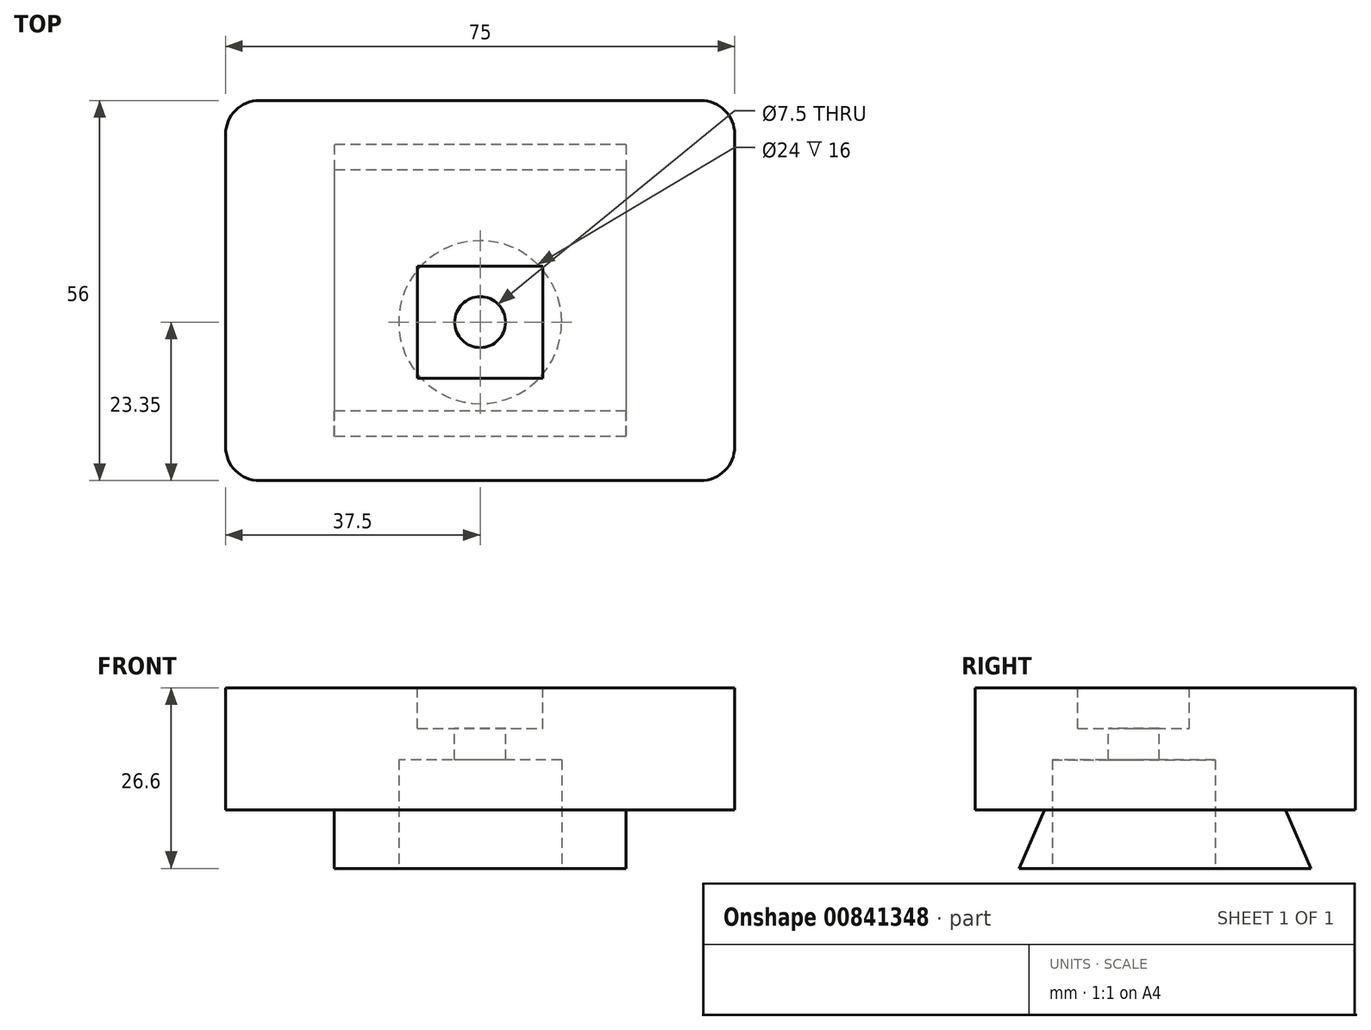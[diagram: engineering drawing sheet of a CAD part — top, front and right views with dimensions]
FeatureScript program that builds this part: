
annotation { "Feature Type Name" : "Feature", "Feature Type Description" : "" }
export const myFeature = defineFeature(function(context is Context, id is Id, definition is map)
    precondition{}
    {
        {
            var Q0;
            Q0=qCreatedBy(makeId("Top.planeOp"),FACE);
            cPlane(context, id + "F0", {"entities" : qUnion([Q0]), "cplaneType" : CPlaneType.OFFSET, "offset" : 8.6 * mm, "oppositeDirection" : true, "width" : 150 * mm, "height" : 150 * mm});
        }
        {
            var Q0;
            Q0=qCreatedBy(makeId("Front.planeOp"),FACE);
            var sketch = newSketch(context, id + "F1", { "sketchPlane" : qUnion([Q0])});
            skLineSegment(sketch, "E0", {"start": v(0, 112.1) * mm, "end": v(0, -117.82) * mm, "construction": true});
            skLineSegment(sketch, "E1", {"start": v(100.36, 0) * mm, "end": v(-122.56, 0) * mm, "construction": true});
            skSolve(sketch);
        }
        {
            var Q0;
            Q0=qCreatedBy(makeId("Top.planeOp"),FACE);
            var sketch = newSketch(context, id + "F2", { "sketchPlane" : qUnion([Q0])});
            skLineSegment(sketch, "E2", {"start": v(0, 30.48) * mm, "end": v(0, -32.87) * mm, "construction": true});
            skLineSegment(sketch, "E3", {"start": v(-42.52, -4.65) * mm, "end": v(39.67, -4.65) * mm, "construction": true});
            skSolve(sketch);
        }
        {
            var Q0;
            Q0=qCreatedBy(id+"F0.planeOp",FACE);
            var sketch = newSketch(context, id + "F3", { "sketchPlane" : qUnion([Q0])});
            skLineSegment(sketch, "E4.bottom", {"start": v(21.5, 21.5) * mm, "end": v(-21.5, 21.5) * mm});
            skLineSegment(sketch, "E4.top", {"start": v(21.5, -21.5) * mm, "end": v(-21.5, -21.5) * mm});
            skLineSegment(sketch, "E4.left", {"start": v(21.5, 21.5) * mm, "end": v(21.5, -21.5) * mm});
            skLineSegment(sketch, "E4.right", {"start": v(-21.5, 21.5) * mm, "end": v(-21.5, -21.5) * mm});
            skPoint(sketch, "E4.middle", {"position": v(0, 0) * mm});
            skSolve(sketch);
        }
        {
            var Q0;
            Q0=qCreatedBy(makeId("Top.planeOp"),FACE);
            var sketch = newSketch(context, id + "F4", { "sketchPlane" : qUnion([Q0])});
            skLineSegment(sketch, "E5.bottom", {"start": v(21.5, 17.75) * mm, "end": v(-21.5, 17.75) * mm});
            skLineSegment(sketch, "E5.top", {"start": v(21.5, -17.75) * mm, "end": v(-21.5, -17.75) * mm});
            skLineSegment(sketch, "E5.left", {"start": v(21.5, 17.75) * mm, "end": v(21.5, -17.75) * mm});
            skLineSegment(sketch, "E5.right", {"start": v(-21.5, 17.75) * mm, "end": v(-21.5, -17.75) * mm});
            skPoint(sketch, "E5.middle", {"position": v(0, 0) * mm});
            skSolve(sketch);
        }
        {
            var Q0;
            Q0 = qSketchRegion(id + "F3", true);
            var Q1;
            Q1 = qSketchRegion(id + "F4", true);
            loft(context, id + "F5", {"sheetProfilesArray" : [{ "sheetProfileEntities" : qUnion([Q0]) }, { "sheetProfileEntities" : qUnion([Q1]) }]});
        }
        {
            var Q0;
            Q0=qCreatedBy(makeId("Top.planeOp"),FACE);
            var sketch = newSketch(context, id + "F6", { "sketchPlane" : qUnion([Q0])});
            skLineSegment(sketch, "E6.bottom", {"start": v(37.5, 28) * mm, "end": v(-37.5, 28) * mm});
            skLineSegment(sketch, "E6.top", {"start": v(37.5, -28) * mm, "end": v(-37.5, -28) * mm});
            skLineSegment(sketch, "E6.left", {"start": v(37.5, 28) * mm, "end": v(37.5, -28) * mm});
            skLineSegment(sketch, "E6.right", {"start": v(-37.5, 28) * mm, "end": v(-37.5, -28) * mm});
            skPoint(sketch, "E6.middle", {"position": v(0, 0) * mm});
            skSolve(sketch);
        }
        {
            var Q0;
            Q0 = qSketchRegion(id + "F6", true);
            extrude(context, id + "F7", {"entities" : qUnion([Q0]), "operationType" : NewBodyOperationType.ADD, "depth" : 18 * mm, "offsetDistance" : 25 * mm});
        }
        {
            var Q0;
            Q0=makeQuery(id+"F7.opExtrude","SWEPT_EDGE",EDGE,{"disambiguationData":[OSD([sQuery(id+"F6.wireOp",EDGE,"E6.bottom"),sQuery(id+"F6.wireOp",EDGE,"E6.right")])]});
            var Q1;
            Q1=makeQuery(id+"F7.opExtrude","SWEPT_EDGE",EDGE,{"disambiguationData":[OSD([sQuery(id+"F6.wireOp",EDGE,"E6.bottom"),sQuery(id+"F6.wireOp",EDGE,"E6.left")])]});
            var Q2;
            Q2=makeQuery(id+"F7.opExtrude","SWEPT_EDGE",EDGE,{"disambiguationData":[OSD([sQuery(id+"F6.wireOp",EDGE,"E6.top"),sQuery(id+"F6.wireOp",EDGE,"E6.left")])]});
            var Q3;
            Q3=makeQuery(id+"F7.opExtrude","SWEPT_EDGE",EDGE,{"disambiguationData":[OSD([sQuery(id+"F6.wireOp",EDGE,"E6.top"),sQuery(id+"F6.wireOp",EDGE,"E6.right")])]});
            fillet(context, id + "F8", {"entities" : qUnion([Q0, Q1, Q2, Q3]), "radius" : 5 * mm, "tangentPropagation" : true, "allowEdgeOverflow" : false});
        }
        {
            var Q0;
            Q0=qCreatedBy(makeId("Top.planeOp"),FACE);
            var sketch = newSketch(context, id + "F9", { "sketchPlane" : qUnion([Q0])});
            skCircle(sketch, "E7", {"center": v(0, -4.65) * mm, "radius": 3.75 * mm});
            skSolve(sketch);
        }
        {
            var Q0;
            Q0 = qSketchRegion(id + "F9", true);
            var Q1;
            Q1=makeQuery(id+"F5.opLoft","CAP_FACE",FACE,{"disambiguationData":[OSD([makeQuery(id+"F3.imprint","IMPRINT",FACE,{"disambiguationData":[TD([[makeQuery(id+"F3.imprint","IMPRINT",EDGE,{"derivedFrom":sQuery(id+"F3.wireOp",EDGE,"E4.bottom")}),1.0]])]})])],"isStart":true});
            var Q2;
            Q2=makeQuery(id+"F7.opExtrude","CAP_FACE",FACE,{"disambiguationData":[OSD([sQuery(id+"F6.wireOp",EDGE,"E6.bottom"),sQuery(id+"F6.wireOp",EDGE,"E6.top"),sQuery(id+"F6.wireOp",EDGE,"E6.left"),sQuery(id+"F6.wireOp",EDGE,"E6.right")])],"isStart":false});
            extrude(context, id + "F10", {"entities" : qUnion([Q0]), "operationType" : NewBodyOperationType.REMOVE, "endBound" : BoundingType.UP_TO_SURFACE, "oppositeDirection" : true, "depth" : 25 * mm, "endBoundEntityFace" : qUnion([Q1]), "offsetDistance" : 25 * mm, "hasSecondDirection" : true, "secondDirectionBound" : SecondDirectionBoundingType.UP_TO_SURFACE, "secondDirectionOppositeDirection" : false, "secondDirectionDepth" : 25 * mm, "secondDirectionBoundEntityFace" : qUnion([Q2])});
        }
        {
            var Q0;
            Q0=qCreatedBy(id+"F0.planeOp",FACE);
            var sketch = newSketch(context, id + "F11", { "sketchPlane" : qUnion([Q0])});
            skCircle(sketch, "E8", {"center": v(0, -4.65) * mm, "radius": 12 * mm});
            skSolve(sketch);
        }
        {
            var Q0;
            Q0 = qSketchRegion(id + "F11", true);
            extrude(context, id + "F12", {"entities" : qUnion([Q0]), "operationType" : NewBodyOperationType.REMOVE, "depth" : 16 * mm, "offsetDistance" : 25 * mm});
        }
        {
            var Q0;
            Q0=makeQuery(id+"F7.opExtrude","CAP_FACE",FACE,{"disambiguationData":[OSD([sQuery(id+"F6.wireOp",EDGE,"E6.bottom"),sQuery(id+"F6.wireOp",EDGE,"E6.top"),sQuery(id+"F6.wireOp",EDGE,"E6.left"),sQuery(id+"F6.wireOp",EDGE,"E6.right")])],"isStart":false});
            var sketch = newSketch(context, id + "F13", { "sketchPlane" : qUnion([Q0])});
            skLineSegment(sketch, "E9.bottom", {"start": v(-9.25, -12.9) * mm, "end": v(9.25, -12.9) * mm});
            skLineSegment(sketch, "E9.top", {"start": v(-9.25, 3.6) * mm, "end": v(9.25, 3.6) * mm});
            skLineSegment(sketch, "E9.left", {"start": v(-9.25, -12.9) * mm, "end": v(-9.25, 3.6) * mm});
            skLineSegment(sketch, "E9.right", {"start": v(9.25, -12.9) * mm, "end": v(9.25, 3.6) * mm});
            skPoint(sketch, "E9.middle", {"position": v(0, -4.65) * mm});
            skSolve(sketch);
        }
        {
            var Q0;
            Q0 = qSketchRegion(id + "F13", true);
            extrude(context, id + "F14", {"entities" : qUnion([Q0]), "operationType" : NewBodyOperationType.REMOVE, "oppositeDirection" : true, "depth" : 6 * mm, "offsetDistance" : 25 * mm});
        }
    });
